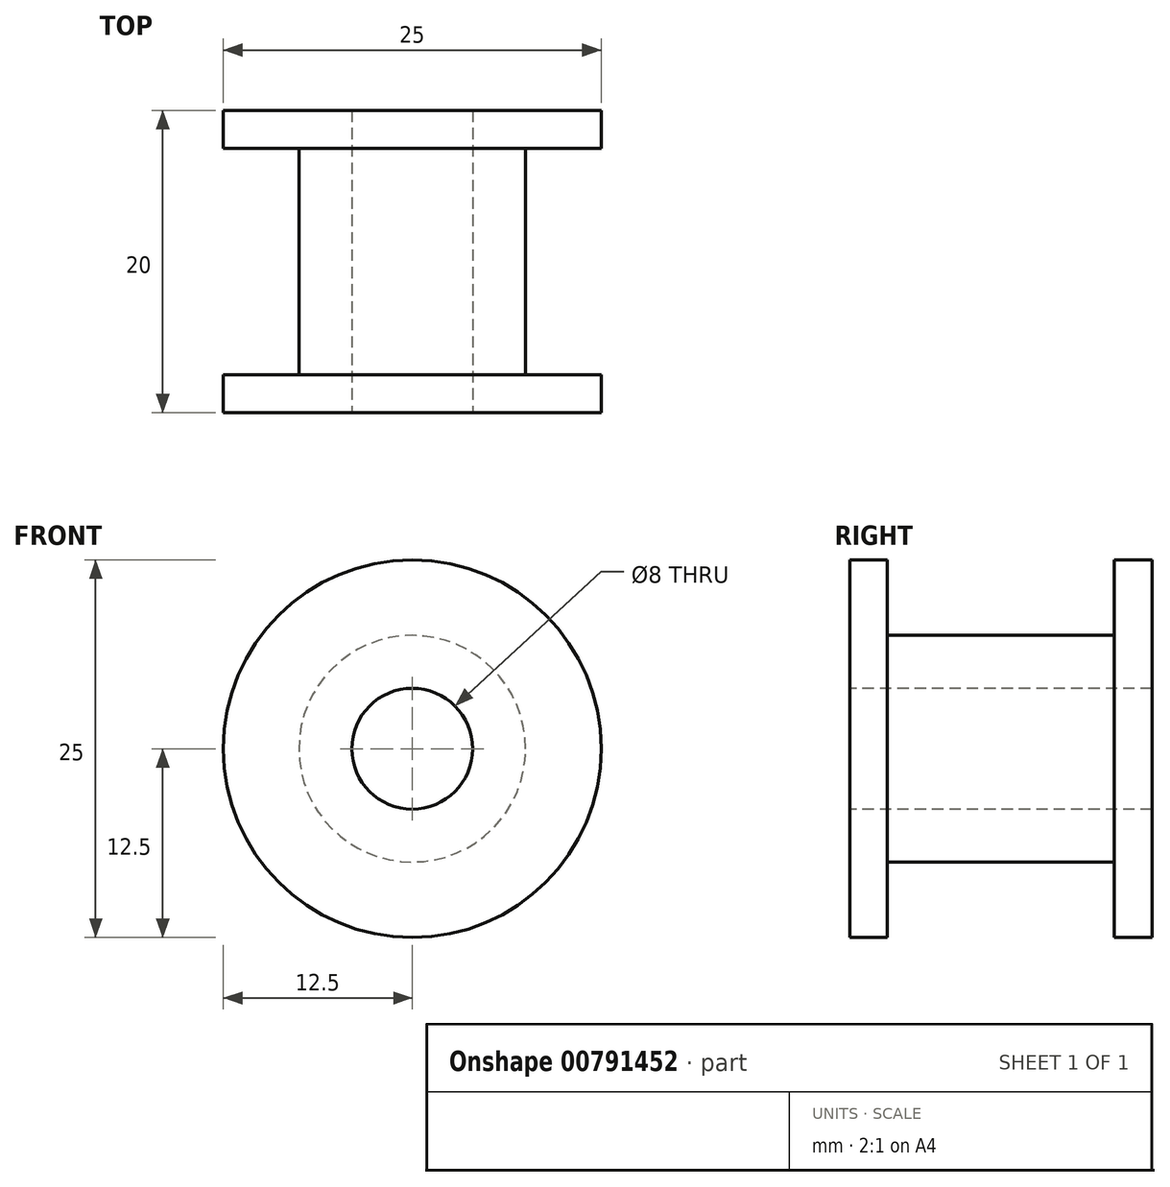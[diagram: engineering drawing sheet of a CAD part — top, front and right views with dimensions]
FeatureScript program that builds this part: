
annotation { "Feature Type Name" : "Feature", "Feature Type Description" : "" }
export const myFeature = defineFeature(function(context is Context, id is Id, definition is map)
    precondition{}
    {
        {
            var Q0;
            Q0=qCreatedBy(makeId("Right.planeOp"),FACE);
            var sketch = newSketch(context, id + "F0", { "sketchPlane" : qUnion([Q0])});
            skLineSegment(sketch, "E0", {"start": v(0, 0) * mm, "end": v(20, 0) * mm});
            skLineSegment(sketch, "E1", {"start": v(20, 0) * mm, "end": v(20, 12.5) * mm});
            skLineSegment(sketch, "E2", {"start": v(20, 12.5) * mm, "end": v(17.5, 12.5) * mm});
            skLineSegment(sketch, "E3", {"start": v(17.5, 12.5) * mm, "end": v(17.5, 7.5) * mm});
            skLineSegment(sketch, "E4", {"start": v(17.5, 7.5) * mm, "end": v(2.5, 7.5) * mm});
            skLineSegment(sketch, "E5", {"start": v(2.5, 7.5) * mm, "end": v(2.5, 12.5) * mm});
            skLineSegment(sketch, "E6", {"start": v(2.5, 12.5) * mm, "end": v(0, 12.5) * mm});
            skLineSegment(sketch, "E7", {"start": v(0, 12.5) * mm, "end": v(0, 0) * mm});
            skSolve(sketch);
        }
        {
            var Q0;
            Q0 = qSketchRegion(id + "F0", true);
            var Q1;
            Q1=sQuery(id+"F0.wireOp",EDGE,"E0");
            revolve(context, id + "F1", {"surfaceOperationType" : NewSurfaceOperationType.NEW, "entities" : qUnion([Q0]), "axis" : qUnion([Q1]), "revolveType" : RevolveType.FULL});
        }
        {
            var Q0;
            Q0=makeQuery(id+"F1.opRevolve","SWEPT_FACE",FACE,{"disambiguationData":[OSD([sQuery(id+"F0.wireOp",EDGE,"E7")])]});
            var sketch = newSketch(context, id + "F2", { "sketchPlane" : qUnion([Q0])});
            skPoint(sketch, "E8", {"position": v(0, 0) * mm});
            skSolve(sketch);
        }
        {
            var Q0;
            Q0=sQuery(id+"F2.wireOp",VERTEX,"E8");
            var Q1;
            Q1=makeQuery(id+"F1.opRevolve","SWEPT_BODY",BODY,{"disambiguationData":[OSD([sQuery(id+"F0.wireOp",EDGE,"E0"),sQuery(id+"F0.wireOp",EDGE,"E1"),sQuery(id+"F0.wireOp",EDGE,"E2"),sQuery(id+"F0.wireOp",EDGE,"E3"),sQuery(id+"F0.wireOp",EDGE,"E4"),sQuery(id+"F0.wireOp",EDGE,"E5"),sQuery(id+"F0.wireOp",EDGE,"E6"),sQuery(id+"F0.wireOp",EDGE,"E7")])]});
            hole(context, id + "F3", {"style" : HoleStyle.SIMPLE, "endStyle" : HoleEndStyle.THROUGH, "holeDiameter" : 8 * mm, "majorDiameter" : 5 * mm, "isTappedThrough" : true, "tappedDepth" : 12 * mm, "tapClearance" : 3, "locations" : qUnion([Q0]), "scope" : qUnion([Q1])});
        }
    });
